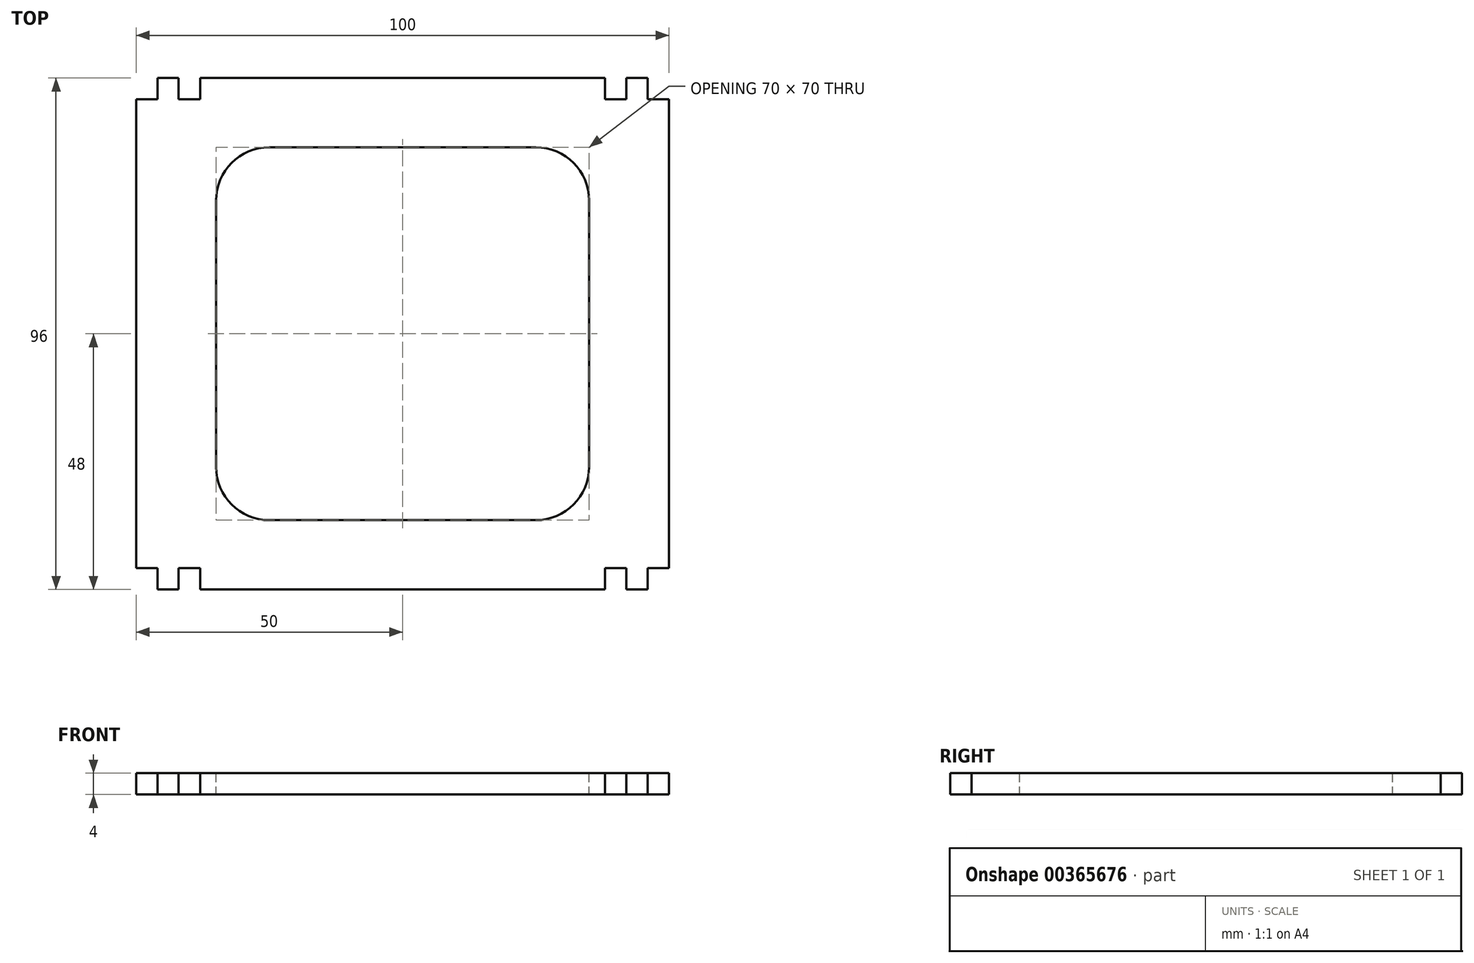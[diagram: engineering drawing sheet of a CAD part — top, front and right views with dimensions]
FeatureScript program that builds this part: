
annotation { "Feature Type Name" : "Feature", "Feature Type Description" : "" }
export const myFeature = defineFeature(function(context is Context, id is Id, definition is map)
    precondition{}
    {
        {
            var Q0;
            Q0=qCreatedBy(makeId("Top.planeOp"),FACE);
            var sketch = newSketch(context, id + "F0", { "sketchPlane" : qUnion([Q0])});
            skLineSegment(sketch, "E0.bottom", {"start": v(0, 0) * mm, "end": v(-100, 0) * mm});
            skLineSegment(sketch, "E0.top", {"start": v(0, 96) * mm, "end": v(-100, 96) * mm});
            skLineSegment(sketch, "E0.left", {"start": v(0, 0) * mm, "end": v(0, 96) * mm});
            skLineSegment(sketch, "E0.right", {"start": v(-100, 0) * mm, "end": v(-100, 96) * mm});
            skSolve(sketch);
        }
        {
            var Q0;
            Q0 = qSketchRegion(id + "F0", true);
            extrude(context, id + "F1", {"entities" : qUnion([Q0]), "depth" : 4 * mm});
        }
        {
            var Q0;
            Q0=makeQuery(id+"F1.opExtrude","CAP_FACE",FACE,{"disambiguationData":[OSD([sQuery(id+"F0.wireOp",EDGE,"E0.bottom"),sQuery(id+"F0.wireOp",EDGE,"E0.top"),sQuery(id+"F0.wireOp",EDGE,"E0.left"),sQuery(id+"F0.wireOp",EDGE,"E0.right")])],"isStart":false});
            var sketch = newSketch(context, id + "F2", { "sketchPlane" : qUnion([Q0])});
            skLineSegment(sketch, "E1", {"start": v(-50, 0) * mm, "end": v(-50, 96) * mm, "construction": true});
            skLineSegment(sketch, "E2", {"start": v(-100, 48) * mm, "end": v(0, 48) * mm, "construction": true});
            skLineSegment(sketch, "E3.bottom", {"start": v(0, 0) * mm, "end": v(-4, 0) * mm});
            skLineSegment(sketch, "E3.top", {"start": v(0, 4) * mm, "end": v(-4, 4) * mm});
            skLineSegment(sketch, "E3.left", {"start": v(0, 0) * mm, "end": v(0, 4) * mm});
            skLineSegment(sketch, "E3.right", {"start": v(-4, 0) * mm, "end": v(-4, 4) * mm});
            skLineSegment(sketch, "E4.bottom", {"start": v(-8, 0) * mm, "end": v(-12, 0) * mm});
            skLineSegment(sketch, "E4.top", {"start": v(-8, 4) * mm, "end": v(-12, 4) * mm});
            skLineSegment(sketch, "E4.left", {"start": v(-8, 0) * mm, "end": v(-8, 4) * mm});
            skLineSegment(sketch, "E4.right", {"start": v(-12, 0) * mm, "end": v(-12, 4) * mm});
            skLineSegment(sketch, "E5.MirrorCS", {"start": v(-4, 96) * mm, "end": v(-4, 92) * mm});
            skLineSegment(sketch, "E6.MirrorCS", {"start": v(-8, 96) * mm, "end": v(-8, 92) * mm});
            skLineSegment(sketch, "E7.MirrorCS", {"start": v(-12, 96) * mm, "end": v(-12, 92) * mm});
            skLineSegment(sketch, "E8.MirrorCS", {"start": v(-8, 96) * mm, "end": v(-12, 96) * mm});
            skLineSegment(sketch, "E9.MirrorCS", {"start": v(0, 96) * mm, "end": v(0, 92) * mm});
            skLineSegment(sketch, "E10.MirrorCS", {"start": v(0, 92) * mm, "end": v(-4, 92) * mm});
            skLineSegment(sketch, "E11.MirrorCS", {"start": v(0, 96) * mm, "end": v(-4, 96) * mm});
            skLineSegment(sketch, "E12.MirrorCS", {"start": v(-8, 92) * mm, "end": v(-12, 92) * mm});
            skLineSegment(sketch, "E13.MirrorCS", {"start": v(-100, 96) * mm, "end": v(-100, 92) * mm});
            skLineSegment(sketch, "E14.MirrorCS", {"start": v(-92, 0) * mm, "end": v(-88, 0) * mm});
            skLineSegment(sketch, "E15.MirrorCS", {"start": v(-96, 0) * mm, "end": v(-96, 4) * mm});
            skLineSegment(sketch, "E16.MirrorCS", {"start": v(-100, 0) * mm, "end": v(-100, 4) * mm});
            skLineSegment(sketch, "E17.MirrorCS", {"start": v(-100, 4) * mm, "end": v(-96, 4) * mm});
            skLineSegment(sketch, "E18.MirrorCS", {"start": v(-100, 0) * mm, "end": v(-96, 0) * mm});
            skLineSegment(sketch, "E19.MirrorCS", {"start": v(-100, 92) * mm, "end": v(-96, 92) * mm});
            skLineSegment(sketch, "E20.MirrorCS", {"start": v(-92, 96) * mm, "end": v(-88, 96) * mm});
            skLineSegment(sketch, "E21.MirrorCS", {"start": v(-92, 4) * mm, "end": v(-88, 4) * mm});
            skLineSegment(sketch, "E22.MirrorCS", {"start": v(-92, 0) * mm, "end": v(-92, 4) * mm});
            skLineSegment(sketch, "E23.MirrorCS", {"start": v(-88, 0) * mm, "end": v(-88, 4) * mm});
            skLineSegment(sketch, "E24.MirrorCS", {"start": v(-96, 96) * mm, "end": v(-96, 92) * mm});
            skLineSegment(sketch, "E25.MirrorCS", {"start": v(-92, 92) * mm, "end": v(-88, 92) * mm});
            skLineSegment(sketch, "E26.MirrorCS", {"start": v(-100, 96) * mm, "end": v(-96, 96) * mm});
            skLineSegment(sketch, "E27.MirrorCS", {"start": v(-92, 96) * mm, "end": v(-92, 92) * mm});
            skLineSegment(sketch, "E28.MirrorCS", {"start": v(-88, 96) * mm, "end": v(-88, 92) * mm});
            skSolve(sketch);
        }
        {
            var Q0;
            Q0 = qSketchRegion(id + "F2", true);
            extrude(context, id + "F3", {"entities" : qUnion([Q0]), "operationType" : NewBodyOperationType.REMOVE, "endBound" : BoundingType.UP_TO_NEXT, "oppositeDirection" : true, "depth" : 25 * mm});
        }
        {
            var Q0;
            Q0=makeQuery(id+"F1.opExtrude","CAP_FACE",FACE,{"disambiguationData":[OSD([sQuery(id+"F0.wireOp",EDGE,"E0.bottom"),sQuery(id+"F0.wireOp",EDGE,"E0.top"),sQuery(id+"F0.wireOp",EDGE,"E0.left"),sQuery(id+"F0.wireOp",EDGE,"E0.right")])],"isStart":false});
            var sketch = newSketch(context, id + "F4", { "sketchPlane" : qUnion([Q0])});
            skLineSegment(sketch, "E29.bottom", {"start": v(-75, 13) * mm, "end": v(-25, 13) * mm});
            skLineSegment(sketch, "E29.top", {"start": v(-75, 83) * mm, "end": v(-25, 83) * mm});
            skLineSegment(sketch, "E29.left", {"start": v(-85, 23) * mm, "end": v(-85, 73) * mm});
            skLineSegment(sketch, "E29.right", {"start": v(-15, 23) * mm, "end": v(-15, 73) * mm});
            skLineSegment(sketch, "E30", {"start": v(-100, 48) * mm, "end": v(0, 48) * mm, "construction": true});
            skLineSegment(sketch, "E31", {"start": v(-50, 0) * mm, "end": v(-50, 96) * mm, "construction": true});
            skLineSegment(sketch, "E32", {"start": v(-50, 83) * mm, "end": v(-50, 13) * mm, "construction": true});
            skLineSegment(sketch, "E33", {"start": v(-85, 48) * mm, "end": v(-15, 48) * mm, "construction": true});
            skPoint(sketch, "E34.visualSharp", {"position": v(-85, 83) * mm});
            skArc(sketch, "E34.filletArc", {"start": v(-75, 83) * mm, "mid": v(-82.07, 80.07) * mm, "end": v(-85, 73) * mm});
            skPoint(sketch, "E35.visualSharp", {"position": v(-15, 83) * mm});
            skArc(sketch, "E35.filletArc", {"start": v(-15, 73) * mm, "mid": v(-17.93, 80.07) * mm, "end": v(-25, 83) * mm});
            skPoint(sketch, "E36.visualSharp", {"position": v(-15, 13) * mm});
            skArc(sketch, "E36.filletArc", {"start": v(-25, 13) * mm, "mid": v(-17.93, 15.93) * mm, "end": v(-15, 23) * mm});
            skPoint(sketch, "E37.visualSharp", {"position": v(-85, 13) * mm});
            skArc(sketch, "E37.filletArc", {"start": v(-85, 23) * mm, "mid": v(-82.07, 15.93) * mm, "end": v(-75, 13) * mm});
            skSolve(sketch);
        }
        {
            var Q0;
            Q0 = qSketchRegion(id + "F4", true);
            extrude(context, id + "F5", {"entities" : qUnion([Q0]), "operationType" : NewBodyOperationType.REMOVE, "endBound" : BoundingType.UP_TO_NEXT, "oppositeDirection" : true, "depth" : 25 * mm});
        }
    });
